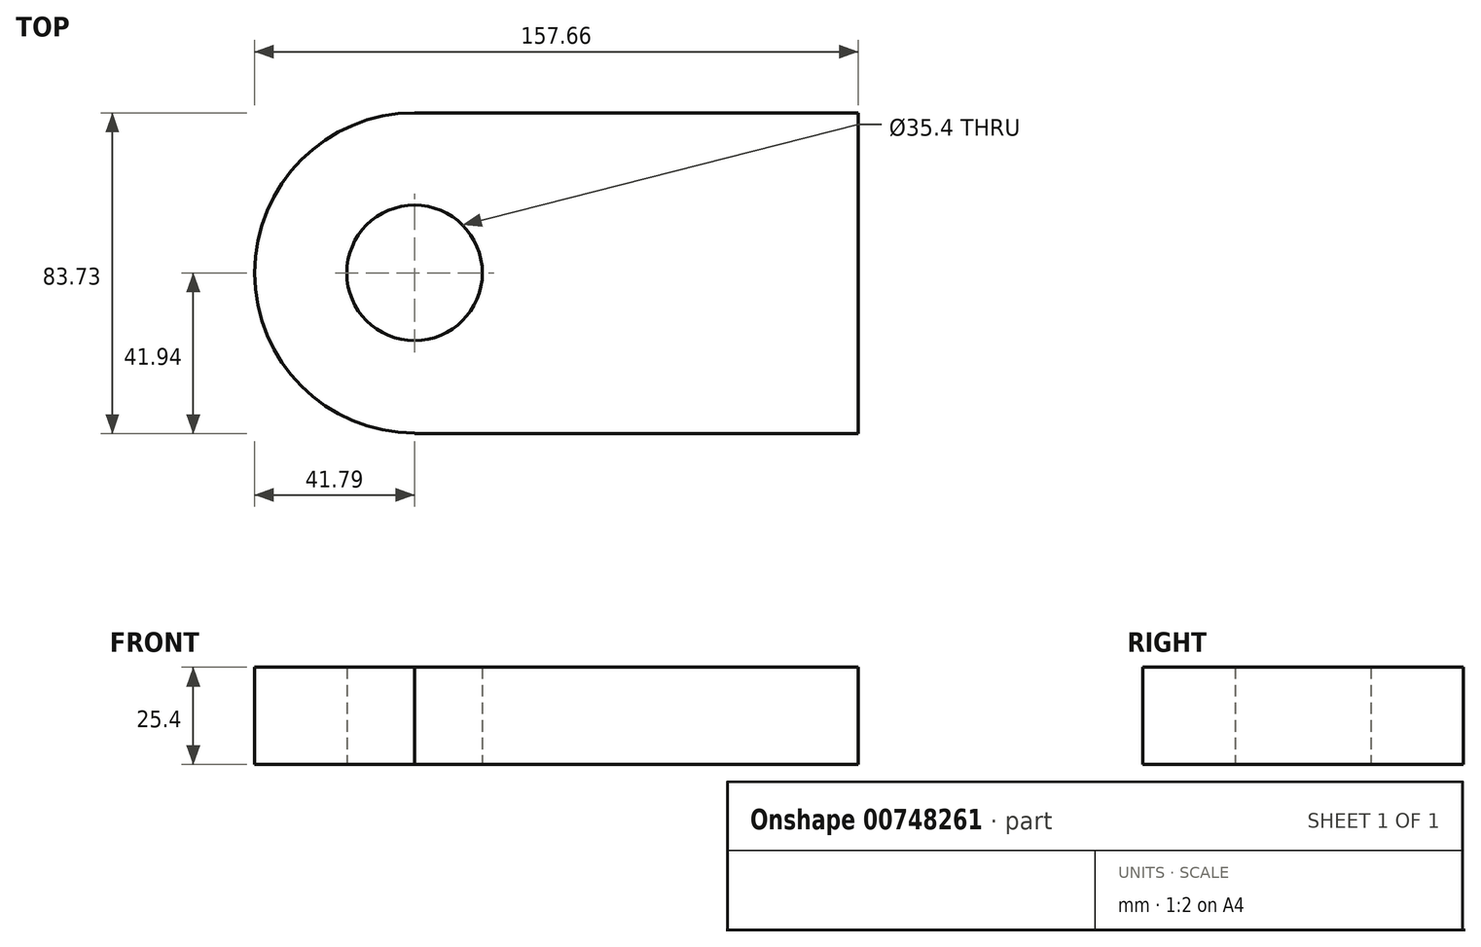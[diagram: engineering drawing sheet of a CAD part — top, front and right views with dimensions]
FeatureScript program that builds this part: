
annotation { "Feature Type Name" : "Feature", "Feature Type Description" : "" }
export const myFeature = defineFeature(function(context is Context, id is Id, definition is map)
    precondition{}
    {
        {
            var Q0;
            Q0=qCreatedBy(makeId("Top.planeOp"),FACE);
            var sketch = newSketch(context, id + "F0", { "sketchPlane" : qUnion([Q0])});
            skCircle(sketch, "E0", {"center": v(0, 0) * mm, "radius": 41.8 * mm});
            skLineSegment(sketch, "E1.bottom", {"start": v(0, 41.8) * mm, "end": v(115.87, 41.8) * mm});
            skLineSegment(sketch, "E1.top", {"start": v(0, -41.94) * mm, "end": v(115.87, -41.94) * mm});
            skLineSegment(sketch, "E1.left", {"start": v(0, 41.8) * mm, "end": v(0, -41.94) * mm});
            skLineSegment(sketch, "E1.right", {"start": v(115.87, 41.8) * mm, "end": v(115.87, -41.94) * mm});
            skCircle(sketch, "E2", {"center": v(0, 0) * mm, "radius": 17.7 * mm});
            skSolve(sketch);
        }
        {
            var Q0;
            {var subQ4=sQuery(id+"F0.wireOp",EDGE,"E1.bottom");Q0=makeQuery(id+"F0.imprint","IMPRINT",FACE,{"disambiguationData":[TD([[makeQuery(id+"F0.imprint","IMPRINT",EDGE,{"derivedFrom":subQ4}),-1.0]])]});}
            var Q1;
            {var subQ0=sQuery(id+"F0.wireOp",EDGE,"E1.left");var subQ1=sQuery(id+"F0.wireOp",EDGE,"E0");var subQ3=makeQuery(id+"F0.imprint","INTERSECT",VERTEX,{"derivedFrom":[subQ1,subQ0]});Q1=makeQuery(id+"F0.imprint","IMPRINT",FACE,{"disambiguationData":[TD([[makeQuery(id+"F0.imprint","IMPRINT",EDGE,{"disambiguationData":[TD([[subQ3,1.0]])],"derivedFrom":subQ0}),1.0]])]});}
            var Q2;
            {var subQ0=sQuery(id+"F0.wireOp",EDGE,"E1.left");var subQ1=sQuery(id+"F0.wireOp",EDGE,"E0");var subQ3=makeQuery(id+"F0.imprint","INTERSECT",VERTEX,{"derivedFrom":[subQ1,subQ0]});Q2=makeQuery(id+"F0.imprint","IMPRINT",FACE,{"disambiguationData":[TD([[makeQuery(id+"F0.imprint","IMPRINT",EDGE,{"disambiguationData":[TD([[subQ3,1.0]])],"derivedFrom":subQ0}),-1.0]])]});}
            extrude(context, id + "F1", {"entities" : qUnion([Q0, Q1, Q2]), "depth" : 25.4 * mm, "offsetDistance" : 25.4 * mm});
        }
        {
            var Q0;
            Q0=makeQuery(id+"F1.opExtrude","CAP_FACE",FACE,{"disambiguationData":[OSD([sQuery(id+"F0.wireOp",EDGE,"E0"),sQuery(id+"F0.wireOp",EDGE,"E1.bottom"),sQuery(id+"F0.wireOp",EDGE,"E1.top"),sQuery(id+"F0.wireOp",EDGE,"E1.left"),sQuery(id+"F0.wireOp",EDGE,"E1.right"),sQuery(id+"F0.wireOp",EDGE,"E2")])],"isStart":false});
            var Q1;
            Q1 = qSketchRegion(id + "F0", true);
            extrude(context, id + "F2", {"entities" : qUnion([Q0, Q1]), "operationType" : NewBodyOperationType.ADD, "depth" : 25.4 * mm, "offsetDistance" : 25.4 * mm});
        }
        {
            var Q0;
            {var subQ0=sQuery(id+"F0.wireOp",EDGE,"E2");var subQ1=sQuery(id+"F0.wireOp",EDGE,"E1.right");var subQ2=sQuery(id+"F0.wireOp",EDGE,"E1.left");var subQ3=sQuery(id+"F0.wireOp",EDGE,"E1.top");var subQ4=sQuery(id+"F0.wireOp",EDGE,"E1.bottom");var subQ5=sQuery(id+"F0.wireOp",EDGE,"E0");Q0=makeQuery(id+"F2.opExtrude","CAP_FACE",FACE,{"disambiguationData":[OSD([subQ5,subQ4,subQ3,subQ2,subQ1,subQ0]),TDD([makeQuery(id+"F1.opExtrude","CAP_FACE",FACE,{"disambiguationData":[OSD([subQ5,subQ4,subQ3,subQ2,subQ1,subQ0])],"isStart":false})])],"isStart":false});}
            extrude(context, id + "F3", {"entities" : qUnion([Q0]), "operationType" : NewBodyOperationType.REMOVE, "oppositeDirection" : true, "depth" : 25.4 * mm, "offsetDistance" : 25.4 * mm});
        }
    });
